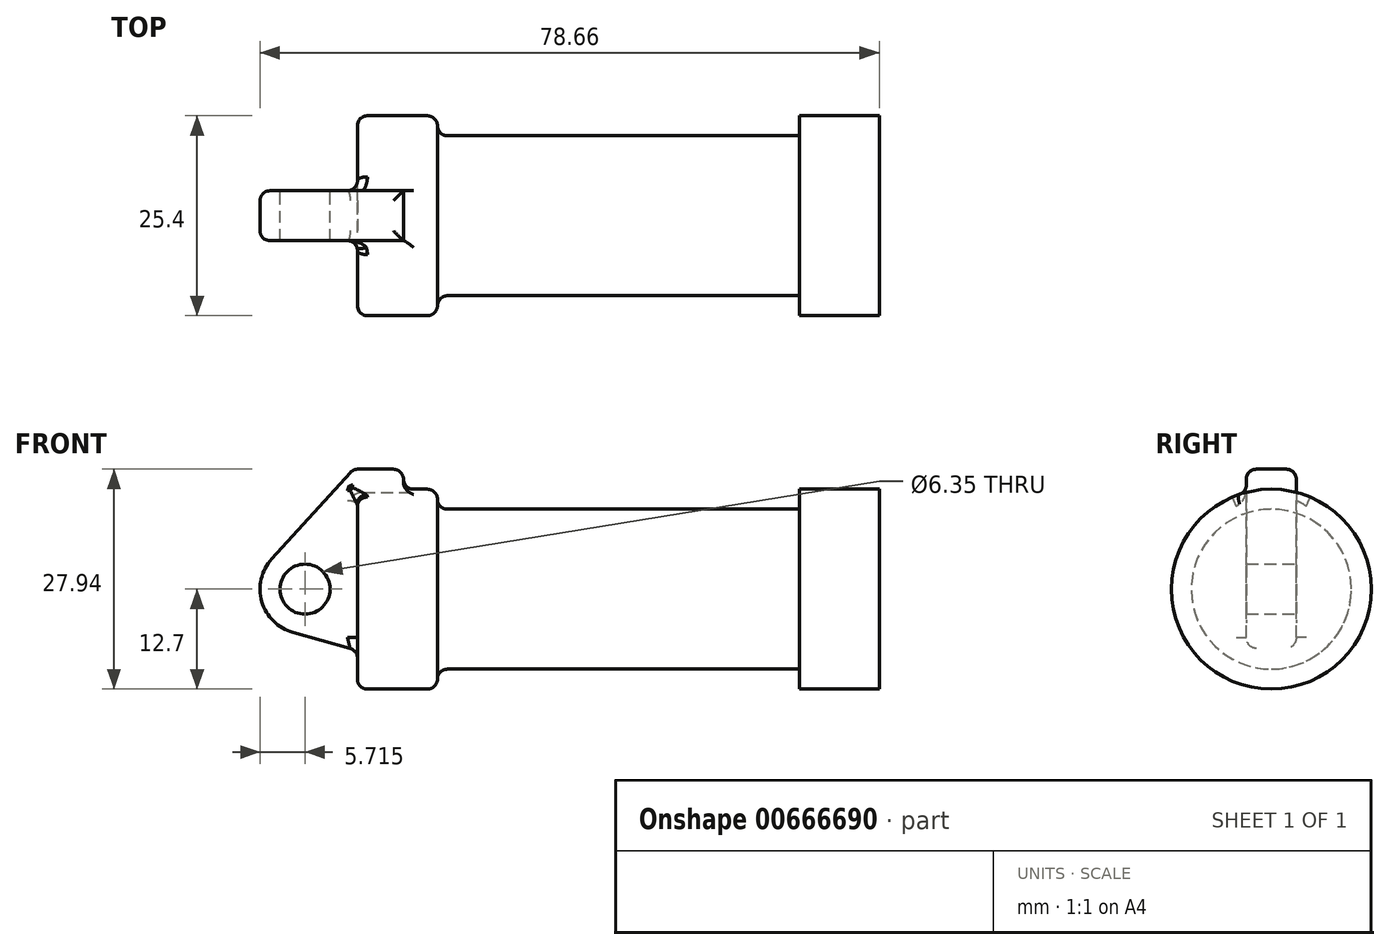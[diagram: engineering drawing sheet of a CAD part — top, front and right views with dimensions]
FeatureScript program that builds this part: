
annotation { "Feature Type Name" : "Feature", "Feature Type Description" : "" }
export const myFeature = defineFeature(function(context is Context, id is Id, definition is map)
    precondition{}
    {
        {
            var Q0;
            Q0=qCreatedBy(makeId("Front.planeOp"),FACE);
            var sketch = newSketch(context, id + "F0", { "sketchPlane" : qUnion([Q0])});
            skLineSegment(sketch, "E0", {"start": v(0, 0) * mm, "end": v(0, 12.7) * mm});
            skLineSegment(sketch, "E1", {"start": v(0, 12.7) * mm, "end": v(10.16, 12.7) * mm});
            skLineSegment(sketch, "E2", {"start": v(10.16, 12.7) * mm, "end": v(10.16, 10.16) * mm});
            skLineSegment(sketch, "E3", {"start": v(10.16, 10.16) * mm, "end": v(56.13, 10.16) * mm});
            skLineSegment(sketch, "E4", {"start": v(56.13, 10.16) * mm, "end": v(56.13, 12.7) * mm});
            skLineSegment(sketch, "E5", {"start": v(56.13, 12.7) * mm, "end": v(66.3, 12.7) * mm});
            skLineSegment(sketch, "E6", {"start": v(66.3, 12.7) * mm, "end": v(66.3, 0) * mm});
            skLineSegment(sketch, "E7", {"start": v(66.3, 0) * mm, "end": v(0, 0) * mm});
            skLineSegment(sketch, "E8", {"start": v(5.84, 15.24) * mm, "end": v(-0.5, 15.24) * mm});
            skLineSegment(sketch, "E9", {"start": v(-0.5, 15.24) * mm, "end": v(-10.88, 3.85) * mm});
            skLineSegment(sketch, "E10", {"start": v(0, 0) * mm, "end": v(-6.65, 0) * mm});
            skCircle(sketch, "E11", {"center": v(-6.65, 0) * mm, "radius": 5.72 * mm});
            skCircle(sketch, "E12", {"center": v(-6.65, 0) * mm, "radius": 3.18 * mm});
            skLineSegment(sketch, "E13", {"start": v(5.84, 15.24) * mm, "end": v(5.84, -9.4) * mm});
            skLineSegment(sketch, "E14", {"start": v(5.84, -9.4) * mm, "end": v(-8.18, -5.5) * mm});
            skSolve(sketch);
        }
        {
            var Q0;
            {var subQ0=sQuery(id+"F0.wireOp",EDGE,"E2");Q0=makeQuery(id+"F0.imprint","IMPRINT",FACE,{"disambiguationData":[TD([[makeQuery(id+"F0.imprint","IMPRINT",EDGE,{"derivedFrom":subQ0}),-1.0]])]});}
            var Q1;
            {var subQ0=sQuery(id+"F0.wireOp",EDGE,"E0");Q1=makeQuery(id+"F0.imprint","IMPRINT",FACE,{"disambiguationData":[TD([[makeQuery(id+"F0.imprint","IMPRINT",EDGE,{"derivedFrom":subQ0}),-1.0]])]});}
            var Q2;
            Q2=sQuery(id+"F0.wireOp",EDGE,"E10");
            revolve(context, id + "F1", {"entities" : qUnion([Q0, Q1]), "axis" : qUnion([Q2]), "revolveType" : RevolveType.FULL});
        }
        {
            var Q0;
            {var subQ0=sQuery(id+"F0.wireOp",EDGE,"E14");Q0=makeQuery(id+"F0.imprint","IMPRINT",FACE,{"disambiguationData":[TD([[makeQuery(id+"F0.imprint","IMPRINT",EDGE,{"derivedFrom":subQ0}),-1.0]])]});}
            var Q1;
            {var subQ5=sQuery(id+"F0.wireOp",EDGE,"E12");Q1=makeQuery(id+"F0.imprint","IMPRINT",FACE,{"disambiguationData":[TD([[makeQuery(id+"F0.imprint","IMPRINT",EDGE,{"derivedFrom":subQ5}),-1.0]])]});}
            var Q2;
            {var subQ1=sQuery(id+"F0.wireOp",EDGE,"E0");Q2=makeQuery(id+"F0.imprint","IMPRINT",FACE,{"disambiguationData":[TD([[makeQuery(id+"F0.imprint","IMPRINT",EDGE,{"derivedFrom":subQ1}),1.0]])]});}
            var Q3;
            {var subQ0=sQuery(id+"F0.wireOp",EDGE,"E0");Q3=makeQuery(id+"F0.imprint","IMPRINT",FACE,{"disambiguationData":[TD([[makeQuery(id+"F0.imprint","IMPRINT",EDGE,{"derivedFrom":subQ0}),-1.0]])]});}
            extrude(context, id + "F2", {"entities" : qUnion([Q0, Q1, Q2, Q3]), "endBound" : BoundingType.SYMMETRIC, "depth" : 6.35 * mm, "offsetDistance" : 25.4 * mm});
        }
        {
            var Q0;
            Q0=makeQuery(id+"F2.opExtrude","CAP_EDGE",EDGE,{"disambiguationData":[OSD([sQuery(id+"F0.wireOp",EDGE,"E9")])],"isStart":false});
            var Q1;
            Q1=makeQuery(id+"F2.opExtrude","CAP_EDGE",EDGE,{"disambiguationData":[OSD([sQuery(id+"F0.wireOp",EDGE,"E8")])],"isStart":false});
            var Q2;
            Q2=makeQuery(id+"F2.opExtrude","SWEPT_EDGE",EDGE,{"disambiguationData":[OSD([sQuery(id+"F0.wireOp",EDGE,"E8"),sQuery(id+"F0.wireOp",EDGE,"E13")])]});
            var Q3;
            Q3=makeQuery(id+"F2.opExtrude","SWEPT_FACE",FACE,{"disambiguationData":[OSD([sQuery(id+"F0.wireOp",EDGE,"E8")])]});
            var Q4;
            Q4=makeQuery(id+"F2.opExtrude","CAP_EDGE",EDGE,{"disambiguationData":[OSD([sQuery(id+"F0.wireOp",EDGE,"E9")])],"isStart":true});
            fillet(context, id + "F3", {"entities" : qUnion([Q0, Q1, Q2, Q3, Q4]), "radius" : 1.27 * mm, "tangentPropagation" : true, "allowEdgeOverflow" : false});
        }
        {
            var Q0;
            Q0=makeQuery(id+"F2.opExtrude","SWEPT_BODY",BODY,{"disambiguationData":[OSD([sQuery(id+"F0.wireOp",EDGE,"E8"),sQuery(id+"F0.wireOp",EDGE,"E9"),sQuery(id+"F0.wireOp",EDGE,"E11"),sQuery(id+"F0.wireOp",EDGE,"E12"),sQuery(id+"F0.wireOp",EDGE,"E13"),sQuery(id+"F0.wireOp",EDGE,"E14")])]});
            var Q1;
            Q1=makeQuery(id+"F1.opRevolve","SWEPT_BODY",BODY,{"disambiguationData":[OSD([sQuery(id+"F0.wireOp",EDGE,"E0"),sQuery(id+"F0.wireOp",EDGE,"E1"),sQuery(id+"F0.wireOp",EDGE,"E2"),sQuery(id+"F0.wireOp",EDGE,"E3"),sQuery(id+"F0.wireOp",EDGE,"E4"),sQuery(id+"F0.wireOp",EDGE,"E5"),sQuery(id+"F0.wireOp",EDGE,"E6"),sQuery(id+"F0.wireOp",EDGE,"E7")])]});
            booleanBodies(context, id + "F4", {"operationType" : BooleanOperationType.UNION, "tools" : qUnion([Q0, Q1])});
        }
        {
            var Q0;
            Q0=makeQuery(id+"F4.opBoolean","INTERSECT",EDGE,{"derivedFrom":[makeQuery(id+"F1.opRevolve","SWEPT_FACE",FACE,{"disambiguationData":[OSD([sQuery(id+"F0.wireOp",EDGE,"E1")])]}),makeQuery(id+"F2.opExtrude","CAP_FACE",FACE,{"disambiguationData":[OSD([sQuery(id+"F0.wireOp",EDGE,"E8"),sQuery(id+"F0.wireOp",EDGE,"E9"),sQuery(id+"F0.wireOp",EDGE,"E11"),sQuery(id+"F0.wireOp",EDGE,"E12"),sQuery(id+"F0.wireOp",EDGE,"E13"),sQuery(id+"F0.wireOp",EDGE,"E14")])],"isStart":false})]});
            var Q1;
            Q1=makeQuery(id+"F4.opBoolean","INTERSECT",EDGE,{"derivedFrom":[makeQuery(id+"F1.opRevolve","SWEPT_FACE",FACE,{"disambiguationData":[OSD([sQuery(id+"F0.wireOp",EDGE,"E0")])]}),makeQuery(id+"F2.opExtrude","CAP_FACE",FACE,{"disambiguationData":[OSD([sQuery(id+"F0.wireOp",EDGE,"E8"),sQuery(id+"F0.wireOp",EDGE,"E9"),sQuery(id+"F0.wireOp",EDGE,"E11"),sQuery(id+"F0.wireOp",EDGE,"E12"),sQuery(id+"F0.wireOp",EDGE,"E13"),sQuery(id+"F0.wireOp",EDGE,"E14")])],"isStart":false})]});
            var Q2;
            Q2=makeQuery(id+"F2.opExtrude","CAP_EDGE",EDGE,{"disambiguationData":[OSD([sQuery(id+"F0.wireOp",EDGE,"E9")])],"isStart":false});
            var Q3;
            Q3=makeQuery(id+"F2.opExtrude","CAP_EDGE",EDGE,{"disambiguationData":[OSD([sQuery(id+"F0.wireOp",EDGE,"E8")])],"isStart":false});
            var Q4;
            Q4=makeQuery(id+"F2.opExtrude","CAP_EDGE",EDGE,{"disambiguationData":[OSD([sQuery(id+"F0.wireOp",EDGE,"E11")])],"isStart":false});
            var Q5;
            Q5=makeQuery(id+"F2.opExtrude","CAP_EDGE",EDGE,{"disambiguationData":[OSD([sQuery(id+"F0.wireOp",EDGE,"E14")])],"isStart":false});
            fillet(context, id + "F5", {"entities" : qUnion([Q0, Q1, Q2, Q3, Q4, Q5]), "radius" : 1.27 * mm, "tangentPropagation" : true, "allowEdgeOverflow" : false});
        }
        {
            var Q0;
            Q0=makeQuery(id+"F4.opBoolean","INTERSECT",EDGE,{"derivedFrom":[makeQuery(id+"F1.opRevolve","SWEPT_FACE",FACE,{"disambiguationData":[OSD([sQuery(id+"F0.wireOp",EDGE,"E1")])]}),makeQuery(id+"F2.opExtrude","SWEPT_FACE",FACE,{"disambiguationData":[OSD([sQuery(id+"F0.wireOp",EDGE,"E13")])]})]});
            var Q1;
            Q1=makeQuery(id+"F1.opRevolve","SWEPT_EDGE",EDGE,{"disambiguationData":[OSD([sQuery(id+"F0.wireOp",EDGE,"E2"),sQuery(id+"F0.wireOp",EDGE,"E3")])]});
            var Q2;
            Q2=makeQuery(id+"F1.opRevolve","SWEPT_EDGE",EDGE,{"disambiguationData":[OSD([sQuery(id+"F0.wireOp",EDGE,"E1"),sQuery(id+"F0.wireOp",EDGE,"E2")])]});
            var Q3;
            Q3=makeQuery(id+"F1.opRevolve","SWEPT_EDGE",EDGE,{"disambiguationData":[OSD([sQuery(id+"F0.wireOp",EDGE,"E0"),sQuery(id+"F0.wireOp",EDGE,"E1")])]});
            fillet(context, id + "F6", {"entities" : qUnion([Q0, Q1, Q2, Q3]), "radius" : 1.27 * mm, "tangentPropagation" : true, "allowEdgeOverflow" : false});
        }
    });
